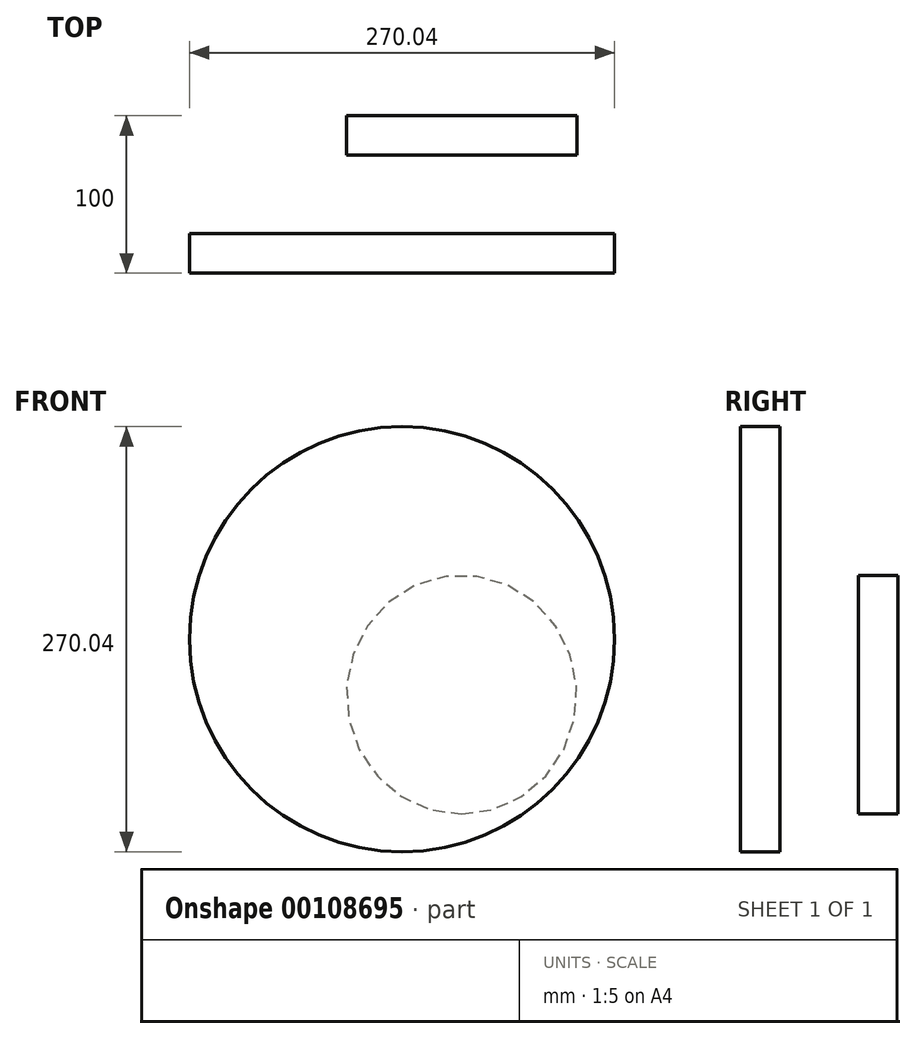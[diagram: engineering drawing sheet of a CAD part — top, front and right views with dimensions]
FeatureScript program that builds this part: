
annotation { "Feature Type Name" : "Feature", "Feature Type Description" : "" }
export const myFeature = defineFeature(function(context is Context, id is Id, definition is map)
    precondition{}
    {
        {
            var Q0;
            Q0=qCreatedBy(makeId("Front.planeOp"),FACE);
            cPlane(context, id + "F0", {"entities" : qUnion([Q0]), "cplaneType" : CPlaneType.OFFSET, "offset" : 75 * mm, "width" : 150 * mm, "height" : 150 * mm});
        }
        {
            var Q0;
            Q0=qCreatedBy(makeId("Front.planeOp"),FACE);
            cPlane(context, id + "F1", {"entities" : qUnion([Q0]), "cplaneType" : CPlaneType.OFFSET, "offset" : 75 * mm, "oppositeDirection" : true, "width" : 150 * mm, "height" : 150 * mm});
        }
        {
            var Q0;
            Q0=qCreatedBy(makeId("Front.planeOp"),FACE);
            var sketch = newSketch(context, id + "F2", { "sketchPlane" : qUnion([Q0])});
            skCircle(sketch, "E0", {"center": v(0, 0) * mm, "radius": 135.02 * mm});
            skSolve(sketch);
        }
        {
            var Q0;
            Q0=qCreatedBy(id+"F1.planeOp",FACE);
            var sketch = newSketch(context, id + "F3", { "sketchPlane" : qUnion([Q0])});
            skEllipse(sketch, "E1", {"center": v(37.8, -35.22) * mm, "majorRadius": 73.19 * mm, "minorRadius": 75.8 * mm, "majorAxis": v(-1, 0)});
            skSolve(sketch);
        }
        {
            var Q0;
            Q0=makeQuery(id+"F2.imprint","IMPRINT",FACE,{"disambiguationData":[TD([[makeQuery(id+"F2.imprint","IMPRINT",EDGE,{"derivedFrom":sQuery(id+"F2.wireOp",EDGE,"E0")}),1.0]])]});
            var Q1;
            Q1=makeQuery(id+"F3.imprint","IMPRINT",FACE,{"disambiguationData":[TD([[makeQuery(id+"F3.imprint","IMPRINT",EDGE,{"derivedFrom":sQuery(id+"F3.wireOp",EDGE,"E1")}),1.0]])]});
            extrude(context, id + "F4", {"entities" : qUnion([Q0, Q1]), "depth" : 25 * mm});
        }
    });
